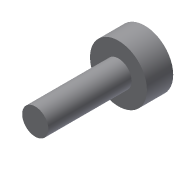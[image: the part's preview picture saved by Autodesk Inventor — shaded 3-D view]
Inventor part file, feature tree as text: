
AUTODESK INVENTOR PART (.ipt)
format: ipt  version: 2014 (Build 180170000, 170)  size: 80,384 bytes
history: native  units: mm
features: revolve x1, sketch x1
ambient origin geometry x8: Origin, YZ Plane, XZ Plane, XY Plane, X Axis, Y Axis, Z Axis, Center Point
bodies: Solid1 (feature_tree)
feature tree (2):
  revolve  "Revolution1"  [1 undecoded]
  sketch  "Sketch1"  dims[d0=19.0mm d1=6.0mm d2=6.5mm d3=3.0mm d4=90.0deg]
note: 1 required parameter value undecoded (feature->parameter linkage not recoverable at this tier; creation-order binding heuristic only, values carry confidence <= 0.55)
